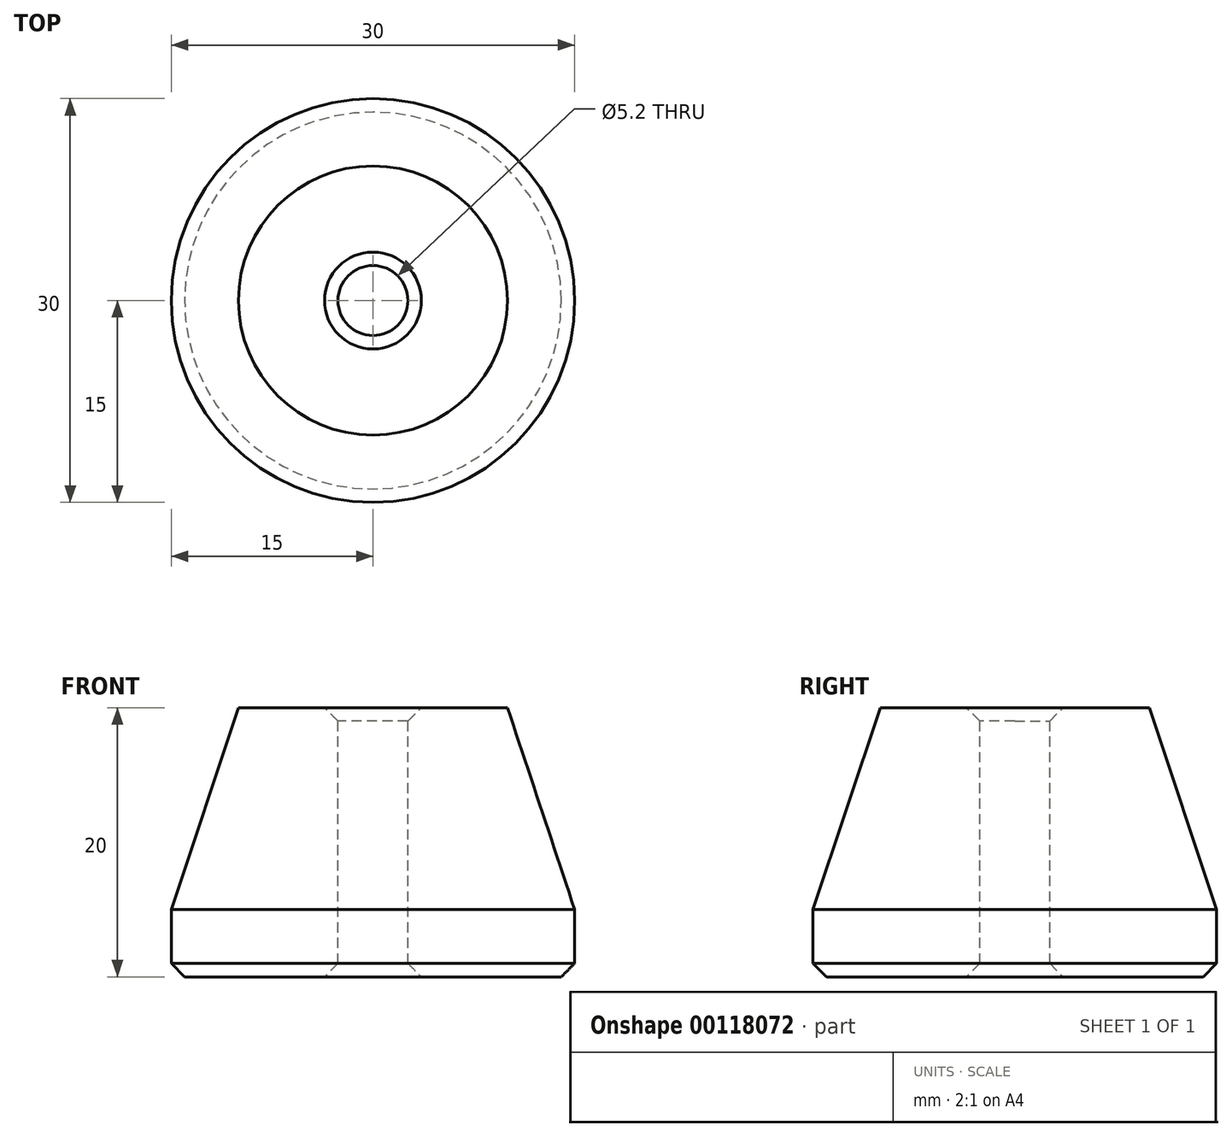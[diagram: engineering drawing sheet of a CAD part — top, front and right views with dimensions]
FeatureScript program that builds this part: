
annotation { "Feature Type Name" : "Feature", "Feature Type Description" : "" }
export const myFeature = defineFeature(function(context is Context, id is Id, definition is map)
    precondition{}
    {
        {
            var Q0;
            Q0=qCreatedBy(makeId("Front.planeOp"),FACE);
            var sketch = newSketch(context, id + "F0", { "sketchPlane" : qUnion([Q0])});
            skLineSegment(sketch, "E0", {"start": v(2.6, 20) * mm, "end": v(2.6, 0) * mm});
            skLineSegment(sketch, "E1", {"start": v(2.6, 0) * mm, "end": v(15, 0) * mm});
            skLineSegment(sketch, "E2", {"start": v(15, 0) * mm, "end": v(15, 5) * mm});
            skLineSegment(sketch, "E3", {"start": v(15, 5) * mm, "end": v(10, 20) * mm});
            skLineSegment(sketch, "E4", {"start": v(10, 20) * mm, "end": v(2.6, 20) * mm});
            skLineSegment(sketch, "E5", {"start": v(0, 20) * mm, "end": v(0, 0) * mm});
            skSolve(sketch);
        }
        {
            var Q0;
            Q0=makeQuery(id+"F0.imprint","IMPRINT",FACE,{"disambiguationData":[TD([[makeQuery(id+"F0.imprint","IMPRINT",EDGE,{"derivedFrom":sQuery(id+"F0.wireOp",EDGE,"E0")}),1.0]])]});
            var Q1;
            Q1=sQuery(id+"F0.wireOp",EDGE,"E5");
            revolve(context, id + "F1", {"entities" : qUnion([Q0]), "axis" : qUnion([Q1]), "revolveType" : RevolveType.FULL});
        }
        {
            var Q0;
            Q0=makeQuery(id+"F1.opRevolve","SWEPT_EDGE",EDGE,{"disambiguationData":[OSD([sQuery(id+"F0.wireOp",EDGE,"E0"),sQuery(id+"F0.wireOp",EDGE,"E4")])]});
            var Q1;
            Q1=makeQuery(id+"F1.opRevolve","SWEPT_EDGE",EDGE,{"disambiguationData":[OSD([sQuery(id+"F0.wireOp",EDGE,"E0"),sQuery(id+"F0.wireOp",EDGE,"E1")])]});
            var Q2;
            Q2=makeQuery(id+"F1.opRevolve","SWEPT_EDGE",EDGE,{"disambiguationData":[OSD([sQuery(id+"F0.wireOp",EDGE,"E1"),sQuery(id+"F0.wireOp",EDGE,"E2")])]});
            chamfer(context, id + "F2", {"entities" : qUnion([Q0, Q1, Q2]), "width" : 1 * mm, "tangentPropagation" : true});
        }
    });
